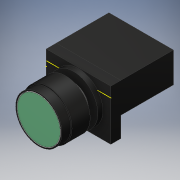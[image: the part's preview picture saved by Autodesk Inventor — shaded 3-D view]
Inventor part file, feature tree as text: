
AUTODESK INVENTOR PART (.ipt)
format: ipt  version: 2019 (Build 230136000, 136)  size: 175,616 bytes
history: native  units: in
note: dims shown in document units (in); Inventor stores cm internally (conversion verified against a paired STEP export)
features: sketch x11, extrude x9, thread x1
ambient origin geometry x8: Origin, YZ Plane, XZ Plane, XY Plane, X Axis, Y Axis, Z Axis, Center Point
bodies: Solid1 (feature_tree)
feature tree (21):
  extrude  "Extrusion1"  Depth=1.305in
  extrude  "Extrusion2"  Depth=1.6in
  sketch  "Sketch3"  dims[d5=0.75in d6=0.25in d7=0.0in]
  sketch  "Sketch7"  dims[d20=0.25in d21=0.0in d22=0.25in d23=0.0in]
  extrude  "Extrusion5"  Depth=0.25in TaperAngle=0.0deg
  extrude  "Extrusion6"  Depth=0.25in TaperAngle=0.0deg
  extrude  "Extrusion7"  Depth=0.75in
  extrude  "Extrusion8"  Depth=0.45in TaperAngle=0.0deg
  extrude  "Extrusion9"  Depth=0.22in TaperAngle=0.0deg
  extrude  "Extrusion10"  [1 undecoded]
  extrude  "Extrusion11"  [1 undecoded]
  thread  "Thread3"  [1 undecoded]
  sketch  "Sketch1"  dims[d0=1.6in d1=1.305in]
  sketch  "Sketch2"  dims[d2=0.75in d3=0.0in d4=1.6in]
  sketch  "Sketch8"  dims[d25=0.125in d26=0.0in d27=0.75in]
  sketch  "Sketch9"  dims[d28=0.19in d29=0.0in d30=0.45in d31=0.0in]
  sketch  "Sketch10"  dims[d32=0.22in d33=0.0in d34=0.22in d35=0.0in]
  sketch  "Sketch11"  dims[d36=1.0in d37=0.0in]
  sketch  "Sketch12"
  sketch  "Sketch13"
  sketch  "Sketch14"
note: 3 required parameter values undecoded (feature->parameter linkage not recoverable at this tier; creation-order binding heuristic only, values carry confidence <= 0.55)
